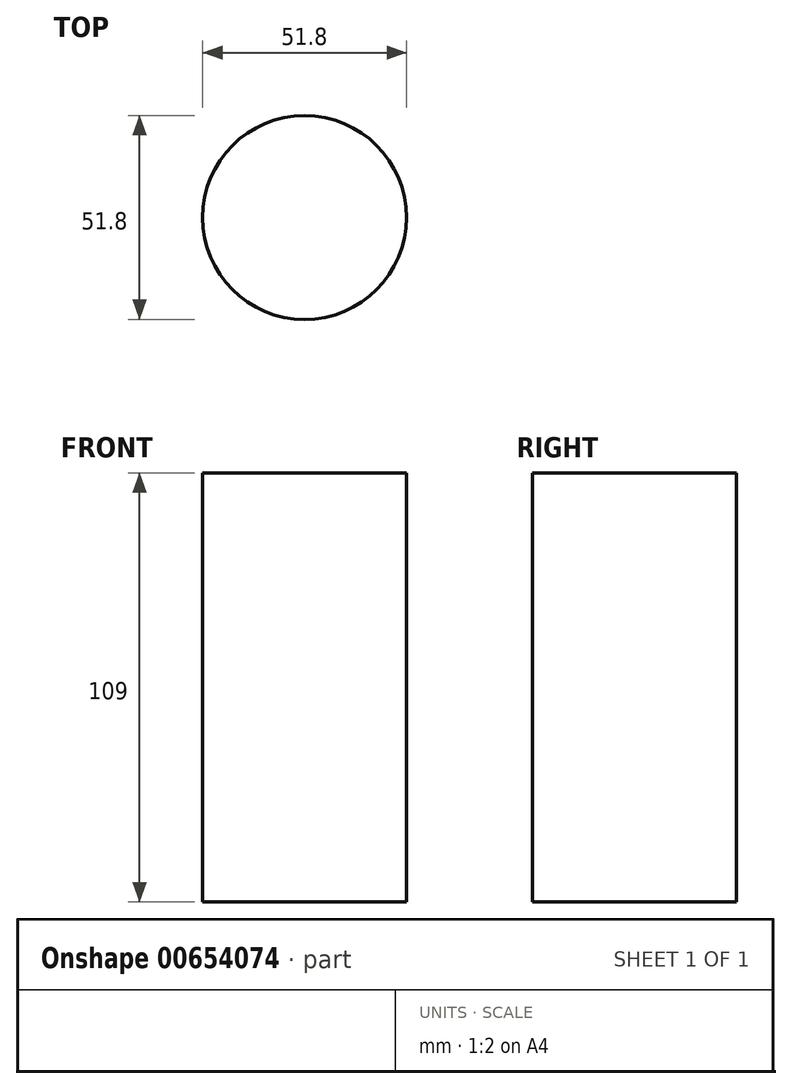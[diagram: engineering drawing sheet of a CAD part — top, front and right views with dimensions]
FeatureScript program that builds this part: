
annotation { "Feature Type Name" : "Feature", "Feature Type Description" : "" }
export const myFeature = defineFeature(function(context is Context, id is Id, definition is map)
    precondition{}
    {
        {
            var Q0;
            Q0=qCreatedBy(makeId("Front.planeOp"),FACE);
            var sketch = newSketch(context, id + "F0", { "sketchPlane" : qUnion([Q0])});
            skLineSegment(sketch, "E0", {"start": v(0, 0) * mm, "end": v(0, 109) * mm});
            skLineSegment(sketch, "E1", {"start": v(0, 109) * mm, "end": v(25.9, 109) * mm});
            skLineSegment(sketch, "E2", {"start": v(25.9, 109) * mm, "end": v(25.9, 0) * mm});
            skLineSegment(sketch, "E3", {"start": v(25.9, 0) * mm, "end": v(0, 0) * mm});
            skSolve(sketch);
        }
        {
            var Q0;
            Q0=makeQuery(id+"F0.imprint","IMPRINT",FACE,{"disambiguationData":[TD([[makeQuery(id+"F0.imprint","IMPRINT",EDGE,{"derivedFrom":sQuery(id+"F0.wireOp",EDGE,"E0")}),-1.0]])]});
            var Q1;
            Q1=sQuery(id+"F0.wireOp",EDGE,"E0");
            revolve(context, id + "F1", {"entities" : qUnion([Q0]), "axis" : qUnion([Q1]), "revolveType" : RevolveType.FULL});
        }
    });
